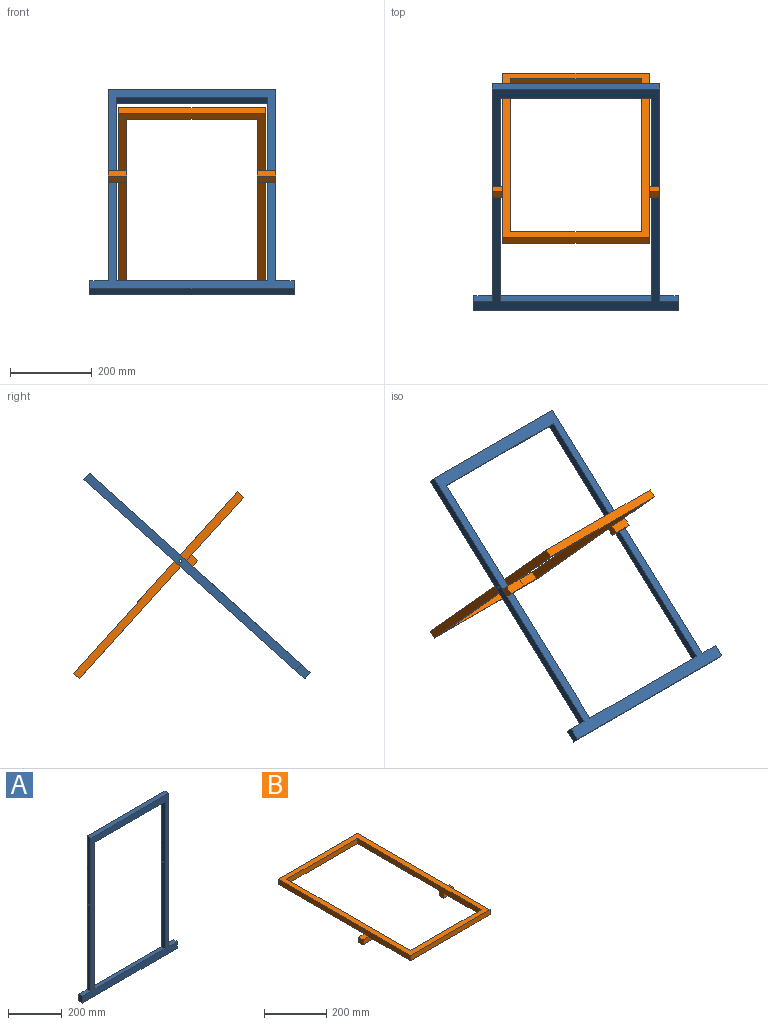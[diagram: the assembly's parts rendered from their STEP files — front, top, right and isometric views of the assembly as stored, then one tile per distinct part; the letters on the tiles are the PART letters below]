
ASSEMBLY  parts=2 mates=1
PART A: 16 faces, bbox 500x20x730 mm
  f0: plane 370x20mm, normal (0,0,1), area 7400mm2, adj f3,f5,f9,f11
  f1: plane 45x20mm, normal (0,0,1), area 900mm2, adj f3,f5,f7,f8
  f2: plane 500x20mm, normal (0,0,-1), area 10000mm2, adj f3,f5,f6,f7
  f3: plane 730x500mm, normal (0,1,0), area 54100mm2, adj f0,f1,f2,f4,f6,f7,f8,f9
  f4: plane 45x20mm, normal (0,0,1), area 900mm2, adj f3,f5,f6,f12
  f5: plane 730x500mm, normal (0,-1,0), area 54100mm2, adj f0,f1,f2,f4,f6,f7,f8,f9
  f6: plane 30x20mm, normal (1,0,0), area 600mm2, adj f2,f3,f4,f5
  f7: plane 30x20mm, normal (-1,0,0), area 600mm2, adj f1,f2,f3,f5
  f8: plane 700x20mm, normal (-1,0,0), area 13971.7mm2, adj f1,f3,f5,f10,f14
  f9: plane 670x20mm, normal (1,0,0), area 13371.7mm2, adj f0,f3,f5,f14,f15
  f10: plane 410x20mm, normal (0,0,1), area 8200mm2, adj f3,f5,f8,f12
  f11: plane 670x20mm, normal (-1,0,0), area 13371.7mm2, adj f0,f3,f5,f13,f15
  f12: plane 700x20mm, normal (1,0,0), area 13971.7mm2, adj f3,f4,f5,f10,f13
  f13: cylinder r=3mm len=20mm, axis (1,0,0), area 377mm2, adj f11,f12
  f14: cylinder r=3mm len=20mm, axis (1,0,0), area 377mm2, adj f8,f9
  f15: plane 370x20mm, normal (0,0,-1), area 7400mm2, adj f3,f5,f9,f11
PART B: 23 faces, bbox 410x600x40 mm
  f0: plane 390x360mm, normal (0,0,-1), area 22000mm2, adj f1,f2,f6,f7,f8,f10,f14,f17
  f1: plane 560x40mm, normal (1,0,0), area 11571.7mm2, adj f0,f3,f4,f9,f10,f12,f14,f15
  f2: plane 600x20mm, normal (-1,0,0), area 11971.7mm2, adj f0,f3,f4,f5,f6,f11,f22
  f3: plane 360x190mm, normal (0,0,-1), area 14000mm2, adj f1,f2,f5,f7,f8,f9,f12,f16
  f4: plane 600x360mm, normal (0,0,1), area 36800mm2, adj f1,f2,f5,f6,f7,f8,f9,f10
  f5: plane 360x20mm, normal (0,-1,0), area 7200mm2, adj f2,f3,f4,f8
  f6: plane 360x20mm, normal (0,1,0), area 7200mm2, adj f0,f2,f4,f8
  f7: plane 560x40mm, normal (-1,0,0), area 11571.7mm2, adj f0,f3,f4,f9,f10,f16,f17,f19
  f8: plane 600x20mm, normal (1,0,0), area 11971.7mm2, adj f0,f3,f4,f5,f6,f20,f21
  f9: plane 320x20mm, normal (0,1,0), area 6400mm2, adj f1,f3,f4,f7
  f10: plane 320x20mm, normal (0,-1,0), area 6400mm2, adj f0,f1,f4,f7
  f11: plane 25x20mm, normal (0,0,1), area 500mm2, adj f2,f12,f13,f14
  f12: plane 45x20mm, normal (0,-1,0), area 900mm2, adj f1,f3,f11,f13,f15
  f13: plane 20x20mm, normal (-1,0,0), area 400mm2, adj f11,f12,f14,f15
  f14: plane 45x20mm, normal (0,1,0), area 900mm2, adj f0,f1,f11,f13,f15
  f15: plane 45x20mm, normal (0,0,-1), area 900mm2, adj f1,f12,f13,f14
  f16: plane 45x20mm, normal (0,-1,0), area 900mm2, adj f3,f7,f18,f19,f20
  f17: plane 45x20mm, normal (0,1,0), area 900mm2, adj f0,f7,f18,f19,f20
  f18: plane 20x20mm, normal (1,0,0), area 400mm2, adj f16,f17,f19,f20
  f19: plane 45x20mm, normal (0,0,-1), area 900mm2, adj f7,f16,f17,f18
  f20: plane 25x20mm, normal (0,0,1), area 500mm2, adj f8,f16,f17,f18
  f21: cylinder r=3mm len=20mm, axis (1,0,0), area 377mm2, adj f7,f8
  f22: cylinder r=3mm len=20mm, axis (1,0,0), area 377mm2, adj f1,f2
PLACE A rot(axis=(-1,0,0),47.9deg) t=(0,0,0)mm
PLACE B rot(axis=(-1,0,0),47.9deg) t=(0,0,0)mm
MATE revolute A.f13 <-> B.f21  axis (1,0,0) through (-185,304.9,289.03)mm
